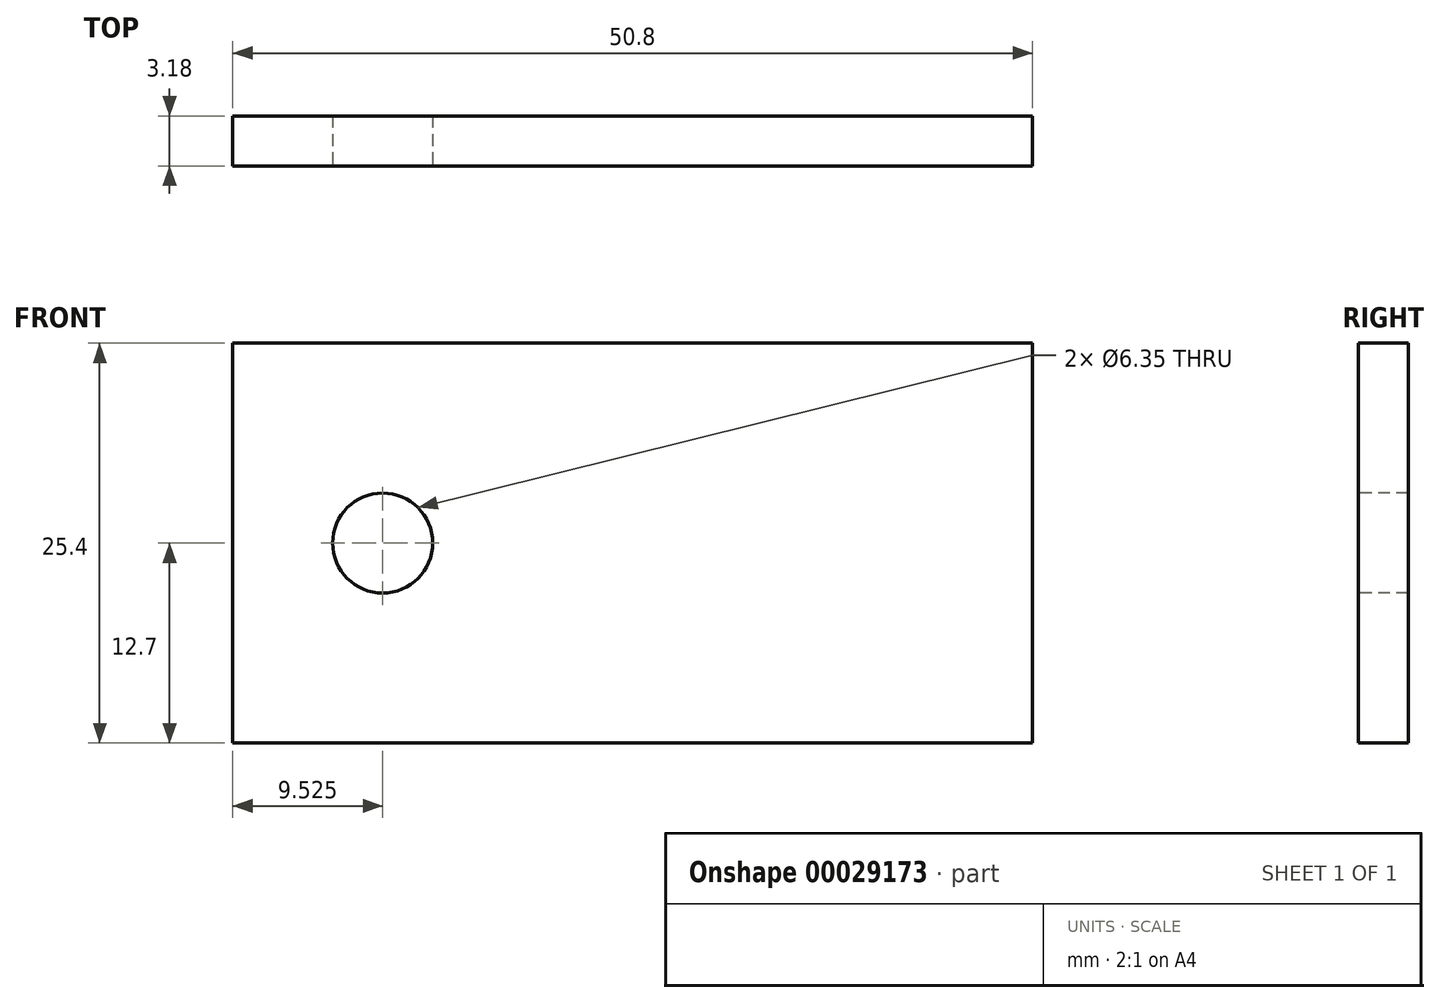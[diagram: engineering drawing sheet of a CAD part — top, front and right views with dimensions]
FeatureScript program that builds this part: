
annotation { "Feature Type Name" : "Feature", "Feature Type Description" : "" }
export const myFeature = defineFeature(function(context is Context, id is Id, definition is map)
    precondition{}
    {
        {
            var Q0;
            Q0=qCreatedBy(makeId("Front.planeOp"),FACE);
            var sketch = newSketch(context, id + "F0", { "sketchPlane" : qUnion([Q0])});
            skLineSegment(sketch, "E0.rect.bottom", {"start": v(25.4, 12.7) * mm, "end": v(-25.4, 12.7) * mm});
            skLineSegment(sketch, "E0.rect.top", {"start": v(25.4, -12.7) * mm, "end": v(-25.4, -12.7) * mm});
            skLineSegment(sketch, "E0.rect.left", {"start": v(25.4, 12.7) * mm, "end": v(25.4, -12.7) * mm});
            skLineSegment(sketch, "E0.rect.right", {"start": v(-25.4, 12.7) * mm, "end": v(-25.4, -12.7) * mm});
            skPoint(sketch, "E0.rect.middle", {"position": v(0, 0) * mm});
            skSolve(sketch);
        }
        {
            var Q0;
            Q0=makeQuery(id+"F0.imprint","IMPRINT",FACE,{"disambiguationData":[TD([[makeQuery(id+"F0.imprint","IMPRINT",EDGE,{"derivedFrom":sQuery(id+"F0.wireOp",EDGE,"E0.rect.bottom")}),1.0]])]});
            extrude(context, id + "F1", {"entities" : qUnion([Q0]), "depth" : 3.17 * mm});
        }
        {
            var Q0;
            Q0=makeQuery(id+"F1.opExtrude","CAP_FACE",FACE,{"disambiguationData":[OSD([sQuery(id+"F0.wireOp",EDGE,"E0.rect.bottom"),sQuery(id+"F0.wireOp",EDGE,"E0.rect.top"),sQuery(id+"F0.wireOp",EDGE,"E0.rect.left"),sQuery(id+"F0.wireOp",EDGE,"E0.rect.right")])],"isStart":false});
            var sketch = newSketch(context, id + "F2", { "sketchPlane" : qUnion([Q0])});
            skLineSegment(sketch, "E1", {"start": v(-25.4, 0) * mm, "end": v(25.4, 0) * mm});
            skCircle(sketch, "E2", {"center": v(-15.88, 0) * mm, "radius": 3.18 * mm});
            skSolve(sketch);
        }
        {
            var Q0;
            Q0 = qSketchRegion(id + "F2", true);
            extrude(context, id + "F3", {"entities" : qUnion([Q0]), "operationType" : NewBodyOperationType.REMOVE, "oppositeDirection" : true, "depth" : 25.4 * mm});
        }
    });
